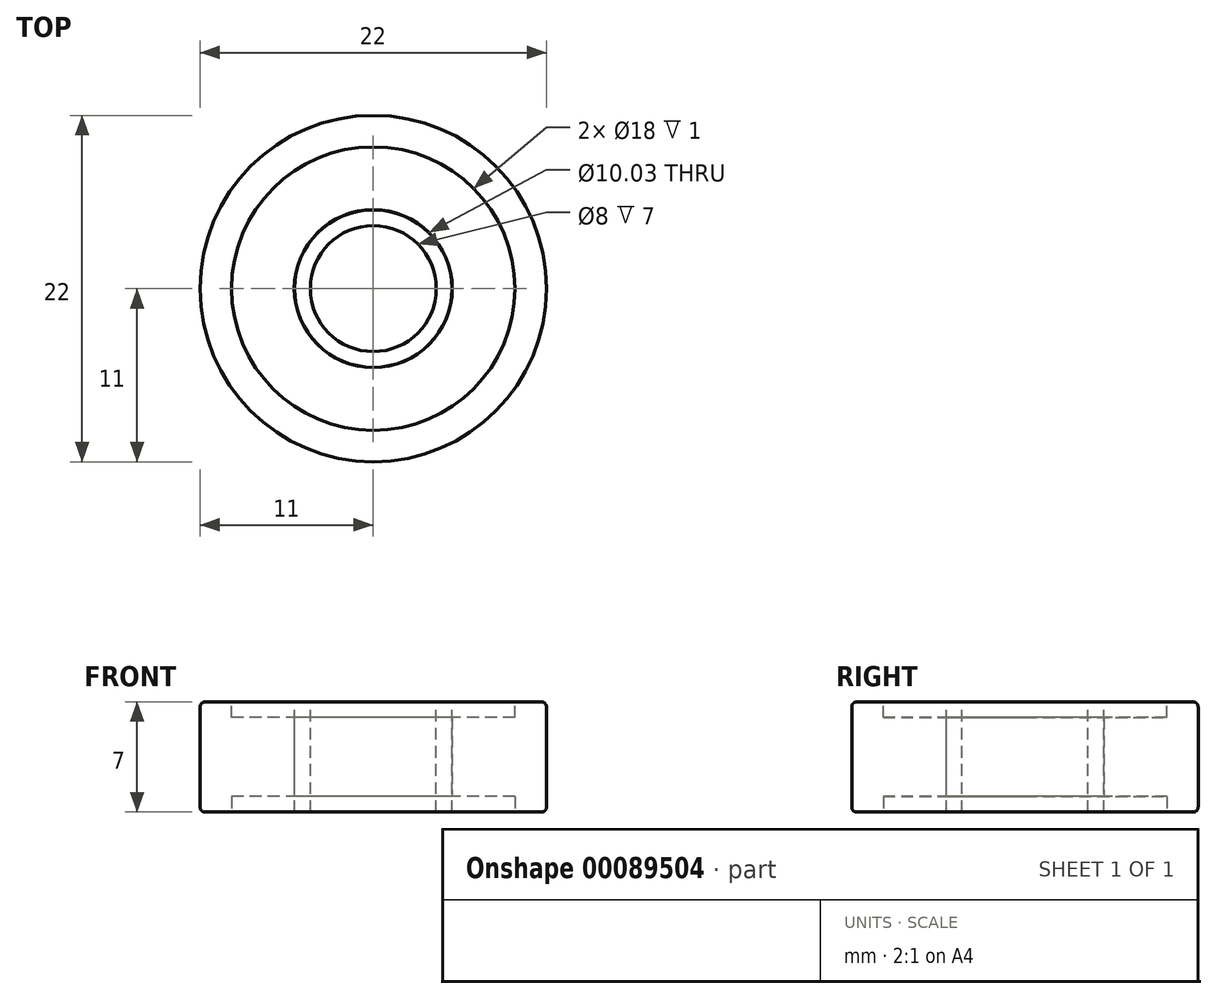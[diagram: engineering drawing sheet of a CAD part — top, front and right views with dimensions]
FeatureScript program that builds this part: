
annotation { "Feature Type Name" : "Feature", "Feature Type Description" : "" }
export const myFeature = defineFeature(function(context is Context, id is Id, definition is map)
    precondition{}
    {
        {
            var Q0;
            Q0=qCreatedBy(makeId("Top.planeOp"),FACE);
            var sketch = newSketch(context, id + "F0", { "sketchPlane" : qUnion([Q0])});
            skCircle(sketch, "E0", {"center": v(0, 0) * mm, "radius": 11 * mm});
            skSolve(sketch);
        }
        {
            var Q0;
            Q0=qSketchRegion(id+"F0",true);
            extrude(context, id + "F1", {"entities" : qUnion([Q0]), "depth" : 3.5 * mm});
        }
        {
            var Q0;
            Q0=makeQuery(id+"F1.opExtrude","CAP_FACE",FACE,{"disambiguationData":[OSD([sQuery(id+"F0.wireOp",EDGE,"E0")])],"isStart":false});
            var sketch = newSketch(context, id + "F2", { "sketchPlane" : qUnion([Q0])});
            skCircle(sketch, "E1", {"center": v(0, 0) * mm, "radius": 9 * mm});
            skCircle(sketch, "E2", {"center": v(0, 0) * mm, "radius": 5 * mm});
            skSolve(sketch);
        }
        {
            var Q0;
            Q0=qSketchRegion(id+"F2",true);
            var Q1;
            Q1=makeQuery(id+"F1.opExtrude","CAP_FACE",FACE,{"disambiguationData":[OSD([sQuery(id+"F0.wireOp",EDGE,"E0")])],"isStart":true});
            extrude(context, id + "F3", {"entities" : qUnion([Q0]), "operationType" : NewBodyOperationType.REMOVE, "endBound" : BoundingType.UP_TO_SURFACE, "oppositeDirection" : true, "endBoundEntityFace" : qUnion([Q1]), "depth" : 25.4 * mm});
        }
        {
            var Q0;
            Q0=makeQuery(id+"F3.boolean.opBoolean","SPLIT",FACE,{"disambiguationData":[TD([makeQuery(id+"F3.opExtrude","SWEPT_FACE",FACE,{"disambiguationData":[OSD([sQuery(id+"F2.wireOp",EDGE,"E2")])]})])],"derivedFrom":makeQuery(id+"F1.opExtrude","CAP_FACE",FACE,{"disambiguationData":[OSD([sQuery(id+"F0.wireOp",EDGE,"E0")])],"isStart":false})});
            var sketch = newSketch(context, id + "F4", { "sketchPlane" : qUnion([Q0])});
            skPoint(sketch, "E3", {"position": v(0, 0) * mm});
            skSolve(sketch);
        }
        {
            var Q0;
            Q0=sQuery(id+"F4.wireOp",VERTEX,"E3");
            var Q1;
            Q1=makeQuery(id+"F3.boolean.opBoolean","SPLIT",BODY,{"disambiguationData":[OD(1.0)],"derivedFrom":makeQuery(id+"F1.opExtrude","SWEPT_BODY",BODY,{"disambiguationData":[OSD([sQuery(id+"F0.wireOp",EDGE,"E0")])]})});
            hole(context, id + "F5", {"style" : HoleStyle.SIMPLE, "holeDiameter" : 8 * mm, "endStyle" : HoleEndStyle.THROUGH, "locations" : qUnion([Q0]), "scope" : qUnion([Q1])});
        }
        {
            var Q0;
            Q0=qCreatedBy(makeId("Top.planeOp"),FACE);
            var sketch = newSketch(context, id + "F6", { "sketchPlane" : qUnion([Q0])});
            skCircle(sketch, "E4", {"center": v(0, 0) * mm, "radius": 9.05 * mm});
            skCircle(sketch, "E5", {"center": v(0, 0) * mm, "radius": 5.02 * mm});
            skSolve(sketch);
        }
        {
            var Q0;
            Q0=qSketchRegion(id+"F6",true);
            extrude(context, id + "F7", {"entities" : qUnion([Q0]), "operationType" : NewBodyOperationType.ADD, "depth" : 2.5 * mm});
        }
        {
            var Q0;
            Q0=makeQuery(id+"F1.opExtrude","CAP_EDGE",EDGE,{"disambiguationData":[OSD([sQuery(id+"F0.wireOp",EDGE,"E0")])],"isStart":false});
            fillet(context, id + "F8", {"entities" : qUnion([Q0]), "radius" : 0.32 * mm, "tangentPropagation" : true, "allowEdgeOverflow" : false});
        }
        {
            var Q0;
            Q0=makeQuery(id+"F3.boolean.opBoolean","SPLIT",BODY,{"disambiguationData":[OD(0.0)],"derivedFrom":makeQuery(id+"F1.opExtrude","SWEPT_BODY",BODY,{"disambiguationData":[OSD([sQuery(id+"F0.wireOp",EDGE,"E0")])]})});
            var Q1;
            Q1=makeQuery(id+"F3.boolean.opBoolean","SPLIT",BODY,{"disambiguationData":[OD(1.0)],"derivedFrom":makeQuery(id+"F1.opExtrude","SWEPT_BODY",BODY,{"disambiguationData":[OSD([sQuery(id+"F0.wireOp",EDGE,"E0")])]})});
            var Q2;
            Q2=qCreatedBy(makeId("Top.planeOp"),FACE);
            mirror(context, id + "F9", {"operationType" : NewBodyOperationType.ADD, "entities" : qUnion([Q0, Q1]), "mirrorPlane" : qUnion([Q2])});
        }
    });
